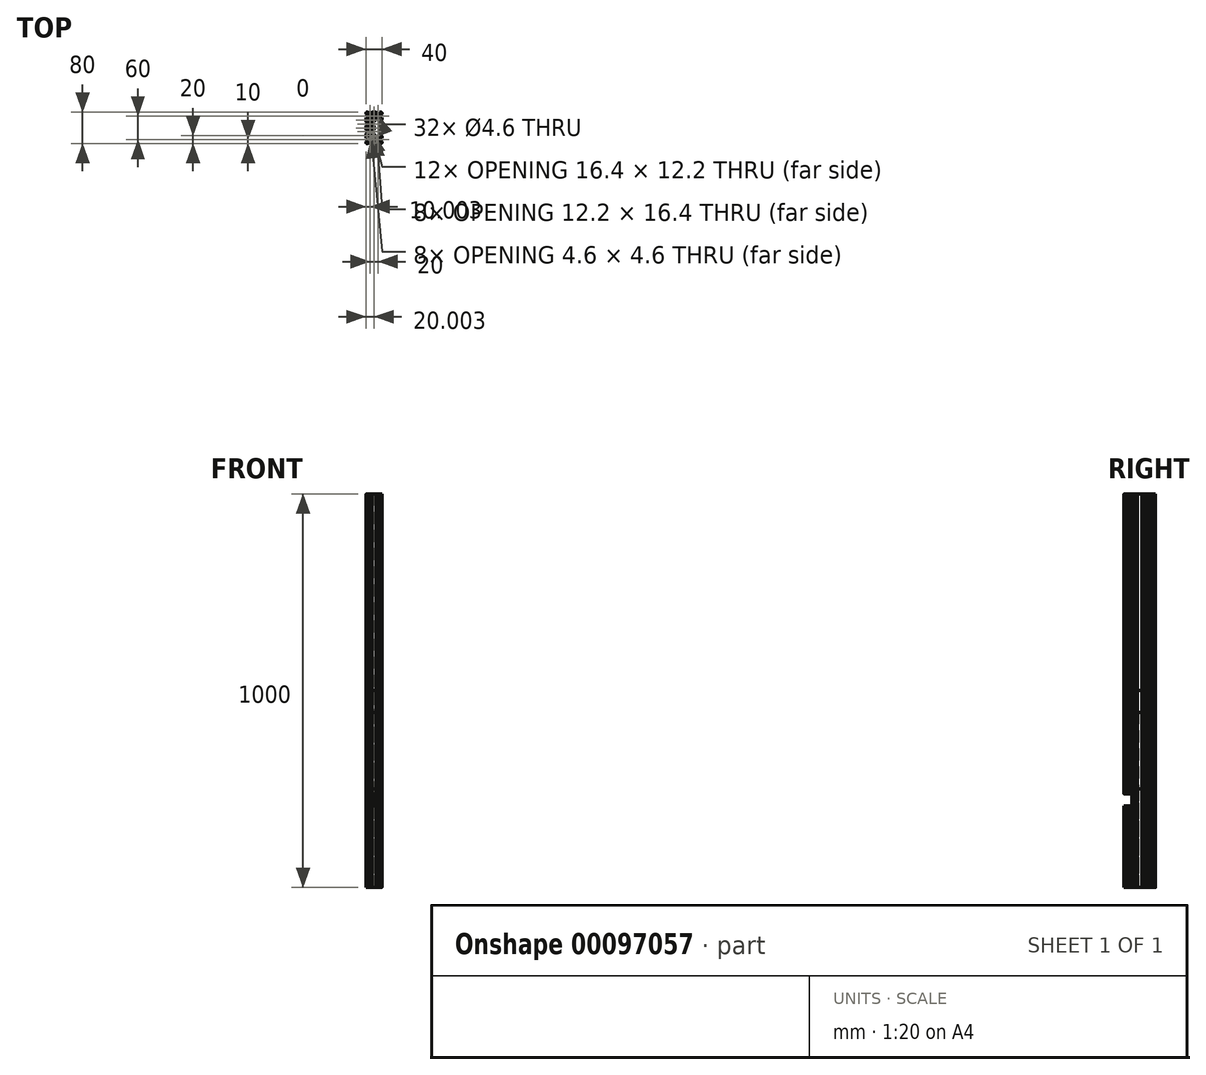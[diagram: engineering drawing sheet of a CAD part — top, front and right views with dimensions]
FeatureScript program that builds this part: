
annotation { "Feature Type Name" : "Feature", "Feature Type Description" : "" }
export const myFeature = defineFeature(function(context is Context, id is Id, definition is map)
    precondition{}
    {
        {
            var Q0;
            Q0=qCreatedBy(makeId("Top.planeOp"),FACE);
            var sketch = newSketch(context, id + "F0", { "sketchPlane" : qUnion([Q0])});
            skLineSegment(sketch, "E0", {"start": v(-12.56, -40) * mm, "end": v(-11.37, -38.82) * mm});
            skLineSegment(sketch, "E1", {"start": v(-11.37, -38.82) * mm, "end": v(-11.37, -38.2) * mm});
            skLineSegment(sketch, "E2", {"start": v(-11.37, -38.2) * mm, "end": v(-13.48, -38.2) * mm});
            skLineSegment(sketch, "E3", {"start": v(-13.48, -38.2) * mm, "end": v(-13.48, -36.56) * mm});
            skLineSegment(sketch, "E4", {"start": v(-13.48, -36.56) * mm, "end": v(-10.82, -33.9) * mm});
            skLineSegment(sketch, "E5", {"start": v(-10.82, -33.9) * mm, "end": v(-8.19, -33.9) * mm});
            skLineSegment(sketch, "E6", {"start": v(-8.19, -33.9) * mm, "end": v(-7.98, -33.69) * mm});
            skLineSegment(sketch, "E7", {"start": v(-7.98, -33.69) * mm, "end": v(-7.77, -33.9) * mm});
            skLineSegment(sketch, "E8", {"start": v(-7.77, -33.9) * mm, "end": v(-5.14, -33.9) * mm});
            skLineSegment(sketch, "E9", {"start": v(-5.14, -33.9) * mm, "end": v(-2.48, -36.56) * mm});
            skLineSegment(sketch, "E10", {"start": v(-2.48, -36.56) * mm, "end": v(-2.48, -38.2) * mm});
            skLineSegment(sketch, "E11", {"start": v(-2.48, -38.2) * mm, "end": v(-4.58, -38.2) * mm});
            skLineSegment(sketch, "E12", {"start": v(-4.58, -38.2) * mm, "end": v(-4.58, -38.82) * mm});
            skLineSegment(sketch, "E13", {"start": v(-4.58, -38.82) * mm, "end": v(-3.4, -40) * mm});
            skLineSegment(sketch, "E14", {"start": v(-3.4, -40) * mm, "end": v(7.44, -40) * mm});
            skLineSegment(sketch, "E15", {"start": v(7.44, -40) * mm, "end": v(8.63, -38.82) * mm});
            skLineSegment(sketch, "E16", {"start": v(8.63, -38.82) * mm, "end": v(8.63, -38.2) * mm});
            skLineSegment(sketch, "E17", {"start": v(8.63, -38.2) * mm, "end": v(6.52, -38.2) * mm});
            skLineSegment(sketch, "E18", {"start": v(6.52, -38.2) * mm, "end": v(6.52, -36.56) * mm});
            skLineSegment(sketch, "E19", {"start": v(6.52, -36.56) * mm, "end": v(9.18, -33.9) * mm});
            skLineSegment(sketch, "E20", {"start": v(9.18, -33.9) * mm, "end": v(11.81, -33.9) * mm});
            skLineSegment(sketch, "E21", {"start": v(11.81, -33.9) * mm, "end": v(12.02, -33.69) * mm});
            skLineSegment(sketch, "E22", {"start": v(12.02, -33.7) * mm, "end": v(12.23, -33.9) * mm});
            skLineSegment(sketch, "E23", {"start": v(12.23, -33.9) * mm, "end": v(14.86, -33.9) * mm});
            skLineSegment(sketch, "E24", {"start": v(14.86, -33.9) * mm, "end": v(17.52, -36.56) * mm});
            skLineSegment(sketch, "E25", {"start": v(17.52, -36.56) * mm, "end": v(17.52, -38.2) * mm});
            skLineSegment(sketch, "E26", {"start": v(17.52, -38.2) * mm, "end": v(15.42, -38.2) * mm});
            skLineSegment(sketch, "E27", {"start": v(15.42, -38.2) * mm, "end": v(15.42, -38.82) * mm});
            skLineSegment(sketch, "E28", {"start": v(15.42, -38.82) * mm, "end": v(16.6, -40) * mm});
            skLineSegment(sketch, "E29", {"start": v(16.6, -40) * mm, "end": v(20.52, -40) * mm});
            skLineSegment(sketch, "E30", {"start": v(22.02, -38.5) * mm, "end": v(22.02, -34.58) * mm});
            skLineSegment(sketch, "E31", {"start": v(22.02, -34.58) * mm, "end": v(20.84, -33.4) * mm});
            skLineSegment(sketch, "E32", {"start": v(20.84, -33.4) * mm, "end": v(20.22, -33.4) * mm});
            skLineSegment(sketch, "E33", {"start": v(20.22, -33.4) * mm, "end": v(20.22, -35.5) * mm});
            skLineSegment(sketch, "E34", {"start": v(20.22, -35.5) * mm, "end": v(18.58, -35.5) * mm});
            skLineSegment(sketch, "E35", {"start": v(18.58, -35.5) * mm, "end": v(15.92, -32.84) * mm});
            skLineSegment(sketch, "E36", {"start": v(15.92, -32.84) * mm, "end": v(15.92, -30.21) * mm});
            skLineSegment(sketch, "E37", {"start": v(15.92, -30.21) * mm, "end": v(15.71, -30) * mm});
            skLineSegment(sketch, "E38", {"start": v(15.71, -30) * mm, "end": v(15.92, -29.79) * mm});
            skLineSegment(sketch, "E39", {"start": v(15.92, -29.79) * mm, "end": v(15.92, -27.16) * mm});
            skLineSegment(sketch, "E40", {"start": v(15.92, -27.16) * mm, "end": v(18.58, -24.5) * mm});
            skLineSegment(sketch, "E41", {"start": v(18.58, -24.5) * mm, "end": v(20.22, -24.5) * mm});
            skLineSegment(sketch, "E42", {"start": v(20.22, -24.5) * mm, "end": v(20.22, -26.6) * mm});
            skLineSegment(sketch, "E43", {"start": v(20.22, -26.6) * mm, "end": v(20.84, -26.6) * mm});
            skLineSegment(sketch, "E44", {"start": v(20.84, -26.6) * mm, "end": v(22.02, -25.42) * mm});
            skLineSegment(sketch, "E45", {"start": v(22.02, -25.42) * mm, "end": v(22.02, -21.5) * mm});
            skLineSegment(sketch, "E46", {"start": v(20.52, -20) * mm, "end": v(16.6, -20) * mm});
            skLineSegment(sketch, "E47", {"start": v(16.6, -20) * mm, "end": v(15.42, -21.18) * mm});
            skLineSegment(sketch, "E48", {"start": v(15.42, -21.18) * mm, "end": v(15.42, -21.8) * mm});
            skLineSegment(sketch, "E49", {"start": v(15.42, -21.8) * mm, "end": v(17.52, -21.8) * mm});
            skLineSegment(sketch, "E50", {"start": v(17.52, -21.8) * mm, "end": v(17.52, -23.44) * mm});
            skLineSegment(sketch, "E51", {"start": v(17.52, -23.44) * mm, "end": v(14.86, -26.1) * mm});
            skLineSegment(sketch, "E52", {"start": v(14.86, -26.1) * mm, "end": v(12.23, -26.1) * mm});
            skLineSegment(sketch, "E53", {"start": v(12.23, -26.1) * mm, "end": v(12.02, -26.3) * mm});
            skLineSegment(sketch, "E54", {"start": v(12.02, -26.3) * mm, "end": v(11.81, -26.1) * mm});
            skLineSegment(sketch, "E55", {"start": v(11.81, -26.1) * mm, "end": v(9.18, -26.1) * mm});
            skLineSegment(sketch, "E56", {"start": v(9.18, -26.1) * mm, "end": v(6.52, -23.44) * mm});
            skLineSegment(sketch, "E57", {"start": v(6.52, -23.44) * mm, "end": v(6.52, -21.8) * mm});
            skLineSegment(sketch, "E58", {"start": v(-12.56, -40) * mm, "end": v(-16.48, -40) * mm});
            skLineSegment(sketch, "E59", {"start": v(6.52, -21.8) * mm, "end": v(8.63, -21.8) * mm});
            skLineSegment(sketch, "E60", {"start": v(-17.98, -38.5) * mm, "end": v(-17.98, -34.58) * mm});
            skLineSegment(sketch, "E61", {"start": v(8.63, -21.8) * mm, "end": v(8.63, -21.18) * mm});
            skLineSegment(sketch, "E62", {"start": v(-17.98, -34.58) * mm, "end": v(-16.8, -33.4) * mm});
            skLineSegment(sketch, "E63", {"start": v(8.63, -21.18) * mm, "end": v(7.44, -20) * mm});
            skLineSegment(sketch, "E64", {"start": v(-16.8, -33.4) * mm, "end": v(-16.18, -33.4) * mm});
            skLineSegment(sketch, "E65", {"start": v(7.44, -20) * mm, "end": v(2.02, -20) * mm});
            skLineSegment(sketch, "E66", {"start": v(-16.18, -33.4) * mm, "end": v(-16.18, -35.5) * mm});
            skLineSegment(sketch, "E67", {"start": v(2.02, -20) * mm, "end": v(2.02, -14.58) * mm});
            skLineSegment(sketch, "E68", {"start": v(-16.18, -35.5) * mm, "end": v(-14.54, -35.5) * mm});
            skLineSegment(sketch, "E69", {"start": v(2.02, -14.58) * mm, "end": v(0.84, -13.4) * mm});
            skLineSegment(sketch, "E70", {"start": v(-14.54, -35.5) * mm, "end": v(-11.88, -32.84) * mm});
            skLineSegment(sketch, "E71", {"start": v(0.84, -13.4) * mm, "end": v(0.22, -13.4) * mm});
            skLineSegment(sketch, "E72", {"start": v(-11.88, -32.84) * mm, "end": v(-11.88, -30.21) * mm});
            skLineSegment(sketch, "E73", {"start": v(0.22, -13.4) * mm, "end": v(0.22, -15.5) * mm});
            skLineSegment(sketch, "E74", {"start": v(-11.88, -30.21) * mm, "end": v(-11.67, -30) * mm});
            skLineSegment(sketch, "E75", {"start": v(0.22, -15.5) * mm, "end": v(-1.42, -15.5) * mm});
            skLineSegment(sketch, "E76", {"start": v(-11.67, -30) * mm, "end": v(-11.88, -29.79) * mm});
            skLineSegment(sketch, "E77", {"start": v(-1.42, -15.5) * mm, "end": v(-4.08, -12.84) * mm});
            skLineSegment(sketch, "E78", {"start": v(-11.88, -29.79) * mm, "end": v(-11.88, -27.16) * mm});
            skLineSegment(sketch, "E79", {"start": v(-4.08, -12.84) * mm, "end": v(-4.08, -10.21) * mm});
            skLineSegment(sketch, "E80", {"start": v(-11.88, -27.16) * mm, "end": v(-14.54, -24.5) * mm});
            skLineSegment(sketch, "E81", {"start": v(-4.08, -10.21) * mm, "end": v(-4.29, -10) * mm});
            skLineSegment(sketch, "E82", {"start": v(-14.54, -24.5) * mm, "end": v(-16.18, -24.5) * mm});
            skLineSegment(sketch, "E83", {"start": v(-4.29, -10) * mm, "end": v(-4.08, -9.8) * mm});
            skLineSegment(sketch, "E84", {"start": v(-16.18, -24.5) * mm, "end": v(-16.18, -26.6) * mm});
            skLineSegment(sketch, "E85", {"start": v(-4.08, -9.8) * mm, "end": v(-4.08, -7.16) * mm});
            skLineSegment(sketch, "E86", {"start": v(-16.18, -26.6) * mm, "end": v(-16.8, -26.6) * mm});
            skLineSegment(sketch, "E87", {"start": v(-4.08, -7.16) * mm, "end": v(-1.42, -4.5) * mm});
            skLineSegment(sketch, "E88", {"start": v(-16.8, -26.6) * mm, "end": v(-17.98, -25.42) * mm});
            skLineSegment(sketch, "E89", {"start": v(-1.42, -4.5) * mm, "end": v(0.22, -4.5) * mm});
            skLineSegment(sketch, "E90", {"start": v(-17.98, -25.42) * mm, "end": v(-17.98, -14.58) * mm});
            skLineSegment(sketch, "E91", {"start": v(0.22, -4.5) * mm, "end": v(0.22, -6.6) * mm});
            skLineSegment(sketch, "E92", {"start": v(-17.98, -14.58) * mm, "end": v(-16.8, -13.4) * mm});
            skLineSegment(sketch, "E93", {"start": v(0.22, -6.6) * mm, "end": v(0.84, -6.6) * mm});
            skLineSegment(sketch, "E94", {"start": v(-16.8, -13.4) * mm, "end": v(-16.18, -13.4) * mm});
            skLineSegment(sketch, "E95", {"start": v(0.84, -6.6) * mm, "end": v(2.02, -5.42) * mm});
            skLineSegment(sketch, "E96", {"start": v(-16.18, -13.4) * mm, "end": v(-16.18, -15.5) * mm});
            skLineSegment(sketch, "E97", {"start": v(2.02, -5.42) * mm, "end": v(2.02, 0) * mm});
            skLineSegment(sketch, "E98", {"start": v(-16.18, -15.5) * mm, "end": v(-14.54, -15.5) * mm});
            skLineSegment(sketch, "E99", {"start": v(-14.54, -15.5) * mm, "end": v(-11.88, -12.84) * mm});
            skLineSegment(sketch, "E100", {"start": v(-11.88, -12.84) * mm, "end": v(-11.88, -10.21) * mm});
            skLineSegment(sketch, "E101", {"start": v(-11.88, -10.21) * mm, "end": v(-11.67, -10) * mm});
            skLineSegment(sketch, "E102", {"start": v(-11.67, -10) * mm, "end": v(-11.88, -9.8) * mm});
            skLineSegment(sketch, "E103", {"start": v(-11.88, -9.8) * mm, "end": v(-11.88, -7.16) * mm});
            skLineSegment(sketch, "E104", {"start": v(-11.88, -7.16) * mm, "end": v(-14.54, -4.5) * mm});
            skLineSegment(sketch, "E105", {"start": v(-14.54, -4.5) * mm, "end": v(-16.18, -4.5) * mm});
            skLineSegment(sketch, "E106", {"start": v(-16.18, -4.5) * mm, "end": v(-16.18, -6.6) * mm});
            skLineSegment(sketch, "E107", {"start": v(-16.18, -6.6) * mm, "end": v(-16.8, -6.6) * mm});
            skLineSegment(sketch, "E108", {"start": v(-16.8, -6.6) * mm, "end": v(-17.98, -5.42) * mm});
            skLineSegment(sketch, "E109", {"start": v(-17.98, -5.42) * mm, "end": v(-17.98, 0) * mm});
            skLineSegment(sketch, "E110", {"start": v(-0.68, -38.2) * mm, "end": v(4.72, -38.2) * mm});
            skLineSegment(sketch, "E111", {"start": v(4.72, -38.2) * mm, "end": v(4.72, -36.24) * mm});
            skLineSegment(sketch, "E112", {"start": v(4.72, -36.24) * mm, "end": v(8.12, -32.84) * mm});
            skLineSegment(sketch, "E113", {"start": v(8.12, -32.84) * mm, "end": v(8.12, -27.16) * mm});
            skLineSegment(sketch, "E114", {"start": v(8.12, -27.16) * mm, "end": v(4.72, -23.76) * mm});
            skLineSegment(sketch, "E115", {"start": v(4.72, -23.76) * mm, "end": v(4.72, -21.8) * mm});
            skLineSegment(sketch, "E116", {"start": v(4.72, -21.8) * mm, "end": v(1.28, -21.8) * mm});
            skLineSegment(sketch, "E117", {"start": v(1.28, -21.8) * mm, "end": v(-4.08, -27.16) * mm});
            skLineSegment(sketch, "E118", {"start": v(-4.08, -27.16) * mm, "end": v(-4.08, -32.84) * mm});
            skLineSegment(sketch, "E119", {"start": v(-4.08, -32.84) * mm, "end": v(-0.68, -36.24) * mm});
            skLineSegment(sketch, "E120", {"start": v(-0.68, -36.24) * mm, "end": v(-0.68, -38.2) * mm});
            skLineSegment(sketch, "E121", {"start": v(-10.82, -26.1) * mm, "end": v(-5.14, -26.1) * mm});
            skLineSegment(sketch, "E122", {"start": v(-5.14, -26.1) * mm, "end": v(0.22, -20.74) * mm});
            skLineSegment(sketch, "E123", {"start": v(0.22, -20.74) * mm, "end": v(0.22, -17.3) * mm});
            skLineSegment(sketch, "E124", {"start": v(0.22, -17.3) * mm, "end": v(-1.74, -17.3) * mm});
            skLineSegment(sketch, "E125", {"start": v(-1.74, -17.3) * mm, "end": v(-5.14, -13.9) * mm});
            skLineSegment(sketch, "E126", {"start": v(-5.14, -13.9) * mm, "end": v(-10.82, -13.9) * mm});
            skLineSegment(sketch, "E127", {"start": v(-10.82, -13.9) * mm, "end": v(-14.22, -17.3) * mm});
            skLineSegment(sketch, "E128", {"start": v(-14.22, -17.3) * mm, "end": v(-16.18, -17.3) * mm});
            skLineSegment(sketch, "E129", {"start": v(-16.18, -17.3) * mm, "end": v(-16.18, -22.7) * mm});
            skLineSegment(sketch, "E130", {"start": v(-16.18, -22.7) * mm, "end": v(-14.22, -22.7) * mm});
            skLineSegment(sketch, "E131", {"start": v(-14.22, -22.7) * mm, "end": v(-10.82, -26.1) * mm});
            skLineSegment(sketch, "E132", {"start": v(-16.18, 0) * mm, "end": v(-16.18, -2.7) * mm});
            skLineSegment(sketch, "E133", {"start": v(-16.18, -2.7) * mm, "end": v(-14.22, -2.7) * mm});
            skLineSegment(sketch, "E134", {"start": v(-14.22, -2.7) * mm, "end": v(-10.82, -6.1) * mm});
            skLineSegment(sketch, "E135", {"start": v(-10.82, -6.1) * mm, "end": v(-5.14, -6.1) * mm});
            skLineSegment(sketch, "E136", {"start": v(-5.14, -6.1) * mm, "end": v(-1.74, -2.7) * mm});
            skLineSegment(sketch, "E137", {"start": v(-1.74, -2.7) * mm, "end": v(0.22, -2.7) * mm});
            skLineSegment(sketch, "E138", {"start": v(0.22, -2.7) * mm, "end": v(0.22, 0) * mm});
            skCircle(sketch, "E139", {"center": v(-7.98, -10) * mm, "radius": 2.3 * mm});
            skPoint(sketch, "E139.first.point", {"position": v(-9.64, -11.59) * mm});
            skPoint(sketch, "E139.second.point", {"position": v(-5.77, -10.63) * mm});
            skPoint(sketch, "E139.third.point", {"position": v(-6.97, -7.93) * mm});
            skCircle(sketch, "E140", {"center": v(-7.98, -30) * mm, "radius": 2.3 * mm});
            skPoint(sketch, "E140.first.point", {"position": v(-10.02, -31.05) * mm});
            skPoint(sketch, "E140.second.point", {"position": v(-6.08, -31.3) * mm});
            skPoint(sketch, "E140.third.point", {"position": v(-6.51, -28.23) * mm});
            skCircle(sketch, "E141", {"center": v(12.02, -30) * mm, "radius": 2.3 * mm});
            skPoint(sketch, "E141.first.point", {"position": v(9.96, -31) * mm});
            skPoint(sketch, "E141.second.point", {"position": v(14.22, -30.67) * mm});
            skPoint(sketch, "E141.third.point", {"position": v(13.22, -28.04) * mm});
            skLineSegment(sketch, "E142", {"start": v(-28.08, 0) * mm, "end": v(32.1, 0) * mm, "construction": true});
            skLineSegment(sketch, "E143.MirrorCS", {"start": v(-8.19, 33.9) * mm, "end": v(-7.98, 33.69) * mm});
            skLineSegment(sketch, "E144.MirrorCS", {"start": v(-11.67, 10) * mm, "end": v(-11.88, 9.79) * mm});
            skLineSegment(sketch, "E145.MirrorCS", {"start": v(-7.98, 33.69) * mm, "end": v(-7.77, 33.9) * mm});
            skLineSegment(sketch, "E146.MirrorCS", {"start": v(-11.88, 10.2) * mm, "end": v(-11.67, 10) * mm});
            skLineSegment(sketch, "E147.MirrorCS", {"start": v(-4.29, 10) * mm, "end": v(-4.08, 9.8) * mm});
            skLineSegment(sketch, "E148.MirrorCS", {"start": v(17.52, 38.2) * mm, "end": v(15.42, 38.2) * mm});
            skLineSegment(sketch, "E149.MirrorCS", {"start": v(-16.18, 4.5) * mm, "end": v(-16.18, 6.6) * mm});
            skLineSegment(sketch, "E150.MirrorCS", {"start": v(-11.88, 30.2) * mm, "end": v(-11.67, 30) * mm});
            skLineSegment(sketch, "E151.MirrorCS", {"start": v(-14.54, 24.5) * mm, "end": v(-16.18, 24.5) * mm});
            skLineSegment(sketch, "E152.MirrorCS", {"start": v(-16.18, 15.5) * mm, "end": v(-14.54, 15.5) * mm});
            skLineSegment(sketch, "E153.MirrorCS", {"start": v(-16.18, 22.7) * mm, "end": v(-14.22, 22.7) * mm});
            skLineSegment(sketch, "E154.MirrorCS", {"start": v(6.52, 38.2) * mm, "end": v(6.52, 36.56) * mm});
            skLineSegment(sketch, "E155.MirrorCS", {"start": v(20.22, 35.5) * mm, "end": v(18.58, 35.5) * mm});
            skLineSegment(sketch, "E156.MirrorCS", {"start": v(17.52, 21.8) * mm, "end": v(17.52, 23.44) * mm});
            skLineSegment(sketch, "E157.MirrorCS", {"start": v(4.72, 23.76) * mm, "end": v(4.72, 21.8) * mm});
            skLineSegment(sketch, "E158.MirrorCS", {"start": v(-16.18, 33.4) * mm, "end": v(-16.18, 35.5) * mm});
            skLineSegment(sketch, "E159.MirrorCS", {"start": v(-1.74, 2.7) * mm, "end": v(0.22, 2.7) * mm});
            skLineSegment(sketch, "E160.MirrorCS", {"start": v(6.52, 23.44) * mm, "end": v(6.52, 21.8) * mm});
            skLineSegment(sketch, "E161.MirrorCS", {"start": v(0.22, 13.4) * mm, "end": v(0.22, 15.5) * mm});
            skLineSegment(sketch, "E162.MirrorCS", {"start": v(-1.42, 4.5) * mm, "end": v(0.22, 4.5) * mm});
            skLineSegment(sketch, "E163.MirrorCS", {"start": v(-14.54, 4.5) * mm, "end": v(-16.18, 4.5) * mm});
            skLineSegment(sketch, "E164.MirrorCS", {"start": v(17.52, 36.56) * mm, "end": v(17.52, 38.2) * mm});
            skLineSegment(sketch, "E165.MirrorCS", {"start": v(18.58, 24.5) * mm, "end": v(20.22, 24.5) * mm});
            skLineSegment(sketch, "E166.MirrorCS", {"start": v(-4.08, 10.21) * mm, "end": v(-4.29, 10) * mm});
            skLineSegment(sketch, "E167.MirrorCS", {"start": v(-16.8, 26.6) * mm, "end": v(-17.98, 25.42) * mm});
            skLineSegment(sketch, "E168.MirrorCS", {"start": v(-4.58, 38.2) * mm, "end": v(-4.58, 38.82) * mm});
            skLineSegment(sketch, "E169.MirrorCS", {"start": v(-2.48, 38.2) * mm, "end": v(-4.58, 38.2) * mm});
            skLineSegment(sketch, "E170.MirrorCS", {"start": v(20.84, 33.4) * mm, "end": v(20.22, 33.4) * mm});
            skLineSegment(sketch, "E171.MirrorCS", {"start": v(-16.8, 33.4) * mm, "end": v(-16.18, 33.4) * mm});
            skLineSegment(sketch, "E172.MirrorCS", {"start": v(15.42, 21.18) * mm, "end": v(15.42, 21.8) * mm});
            skLineSegment(sketch, "E173.MirrorCS", {"start": v(-13.48, 38.2) * mm, "end": v(-13.48, 36.56) * mm});
            skLineSegment(sketch, "E174.MirrorCS", {"start": v(-11.37, 38.82) * mm, "end": v(-11.37, 38.2) * mm});
            skLineSegment(sketch, "E175.MirrorCS", {"start": v(-12.56, 40) * mm, "end": v(-11.37, 38.82) * mm});
            skLineSegment(sketch, "E176.MirrorCS", {"start": v(0.84, 13.4) * mm, "end": v(0.22, 13.4) * mm});
            skLineSegment(sketch, "E177.MirrorCS", {"start": v(7.44, 40) * mm, "end": v(8.63, 38.82) * mm});
            skLineSegment(sketch, "E178.MirrorCS", {"start": v(-4.58, 38.82) * mm, "end": v(-3.4, 40) * mm});
            skLineSegment(sketch, "E179.MirrorCS", {"start": v(-16.18, 13.4) * mm, "end": v(-16.18, 15.5) * mm});
            skLineSegment(sketch, "E180.MirrorCS", {"start": v(-14.22, 17.3) * mm, "end": v(-16.18, 17.3) * mm});
            skLineSegment(sketch, "E181.MirrorCS", {"start": v(-16.18, 26.6) * mm, "end": v(-16.8, 26.6) * mm});
            skLineSegment(sketch, "E182.MirrorCS", {"start": v(4.72, 38.2) * mm, "end": v(4.72, 36.24) * mm});
            skLineSegment(sketch, "E183.MirrorCS", {"start": v(0.84, 6.6) * mm, "end": v(2.02, 5.42) * mm});
            skLineSegment(sketch, "E184.MirrorCS", {"start": v(22.02, 34.58) * mm, "end": v(20.84, 33.4) * mm});
            skLineSegment(sketch, "E185.MirrorCS", {"start": v(12.02, 26.3) * mm, "end": v(11.81, 26.1) * mm});
            skLineSegment(sketch, "E186.MirrorCS", {"start": v(15.71, 30) * mm, "end": v(15.92, 29.79) * mm});
            skLineSegment(sketch, "E187.MirrorCS", {"start": v(8.63, 21.18) * mm, "end": v(7.44, 20) * mm});
            skLineSegment(sketch, "E188.MirrorCS", {"start": v(-11.67, 30) * mm, "end": v(-11.88, 29.79) * mm});
            skLineSegment(sketch, "E189.MirrorCS", {"start": v(-16.8, 6.6) * mm, "end": v(-17.98, 5.42) * mm});
            skLineSegment(sketch, "E190.MirrorCS", {"start": v(20.84, 26.6) * mm, "end": v(22.02, 25.42) * mm});
            skLineSegment(sketch, "E191.MirrorCS", {"start": v(8.63, 21.8) * mm, "end": v(8.63, 21.18) * mm});
            skLineSegment(sketch, "E192.MirrorCS", {"start": v(-16.18, 35.5) * mm, "end": v(-14.54, 35.5) * mm});
            skLineSegment(sketch, "E193.MirrorCS", {"start": v(0.22, 4.5) * mm, "end": v(0.22, 6.6) * mm});
            skLineSegment(sketch, "E194.MirrorCS", {"start": v(-16.18, 6.6) * mm, "end": v(-16.8, 6.6) * mm});
            skLineSegment(sketch, "E195.MirrorCS", {"start": v(20.22, 26.6) * mm, "end": v(20.84, 26.6) * mm});
            skLineSegment(sketch, "E196.MirrorCS", {"start": v(8.63, 38.2) * mm, "end": v(6.52, 38.2) * mm});
            skLineSegment(sketch, "E197.MirrorCS", {"start": v(15.42, 21.8) * mm, "end": v(17.52, 21.8) * mm});
            skLineSegment(sketch, "E198.MirrorCS", {"start": v(20.22, 33.4) * mm, "end": v(20.22, 35.5) * mm});
            skLineSegment(sketch, "E199.MirrorCS", {"start": v(-0.68, 36.24) * mm, "end": v(-0.68, 38.2) * mm});
            skLineSegment(sketch, "E200.MirrorCS", {"start": v(-2.48, 36.56) * mm, "end": v(-2.48, 38.2) * mm});
            skLineSegment(sketch, "E201.MirrorCS", {"start": v(8.63, 38.82) * mm, "end": v(8.63, 38.2) * mm});
            skLineSegment(sketch, "E202.MirrorCS", {"start": v(-11.37, 38.2) * mm, "end": v(-13.48, 38.2) * mm});
            skLineSegment(sketch, "E203.MirrorCS", {"start": v(12.02, 33.69) * mm, "end": v(12.23, 33.9) * mm});
            skLineSegment(sketch, "E204.MirrorCS", {"start": v(16.6, 20) * mm, "end": v(15.42, 21.18) * mm});
            skLineSegment(sketch, "E205.MirrorCS", {"start": v(-16.18, 2.7) * mm, "end": v(-14.22, 2.7) * mm});
            skLineSegment(sketch, "E206.MirrorCS", {"start": v(12.23, 26.1) * mm, "end": v(12.02, 26.3) * mm});
            skLineSegment(sketch, "E207.MirrorCS", {"start": v(-17.98, 14.58) * mm, "end": v(-16.8, 13.4) * mm});
            skLineSegment(sketch, "E208.MirrorCS", {"start": v(15.42, 38.82) * mm, "end": v(16.6, 40) * mm});
            skLineSegment(sketch, "E209.MirrorCS", {"start": v(20.22, 24.5) * mm, "end": v(20.22, 26.6) * mm});
            skLineSegment(sketch, "E210.MirrorCS", {"start": v(6.52, 21.8) * mm, "end": v(8.63, 21.8) * mm});
            skLineSegment(sketch, "E211.MirrorCS", {"start": v(0.22, 15.5) * mm, "end": v(-1.42, 15.5) * mm});
            skLineSegment(sketch, "E212.MirrorCS", {"start": v(-16.8, 13.4) * mm, "end": v(-16.18, 13.4) * mm});
            skLineSegment(sketch, "E213.MirrorCS", {"start": v(11.81, 33.9) * mm, "end": v(12.02, 33.69) * mm});
            skLineSegment(sketch, "E214.MirrorCS", {"start": v(15.92, 30.21) * mm, "end": v(15.71, 30) * mm});
            skLineSegment(sketch, "E215.MirrorCS", {"start": v(2.02, 14.58) * mm, "end": v(0.84, 13.4) * mm});
            skLineSegment(sketch, "E216.MirrorCS", {"start": v(-17.98, 34.58) * mm, "end": v(-16.8, 33.4) * mm});
            skLineSegment(sketch, "E217.MirrorCS", {"start": v(0.22, 17.3) * mm, "end": v(-1.74, 17.3) * mm});
            skLineSegment(sketch, "E218.MirrorCS", {"start": v(-16.18, 24.5) * mm, "end": v(-16.18, 26.6) * mm});
            skLineSegment(sketch, "E219.MirrorCS", {"start": v(0.22, 6.6) * mm, "end": v(0.84, 6.6) * mm});
            skLineSegment(sketch, "E220.MirrorCS", {"start": v(15.42, 38.2) * mm, "end": v(15.42, 38.82) * mm});
            skLineSegment(sketch, "E221.MirrorCS", {"start": v(-17.98, 25.42) * mm, "end": v(-17.98, 14.58) * mm});
            skLineSegment(sketch, "E222.MirrorCS", {"start": v(-12.56, 40) * mm, "end": v(-16.48, 40) * mm});
            skLineSegment(sketch, "E223.MirrorCS", {"start": v(0.22, 2.7) * mm, "end": v(0.22, 0) * mm});
            skLineSegment(sketch, "E224.MirrorCS", {"start": v(-5.14, 26.1) * mm, "end": v(0.22, 20.74) * mm});
            skPoint(sketch, "E225.MirrorP", {"position": v(13.22, 28.04) * mm});
            skLineSegment(sketch, "E226.MirrorCS", {"start": v(2.02, 20) * mm, "end": v(2.02, 14.58) * mm});
            skLineSegment(sketch, "E227.MirrorCS", {"start": v(17.52, 23.44) * mm, "end": v(14.86, 26.1) * mm});
            skLineSegment(sketch, "E228.MirrorCS", {"start": v(8.12, 27.16) * mm, "end": v(4.72, 23.76) * mm});
            skLineSegment(sketch, "E229.MirrorCS", {"start": v(18.58, 35.5) * mm, "end": v(15.92, 32.84) * mm});
            skLineSegment(sketch, "E230.MirrorCS", {"start": v(6.52, 36.56) * mm, "end": v(9.18, 33.9) * mm});
            skLineSegment(sketch, "E231.MirrorCS", {"start": v(-14.22, 22.7) * mm, "end": v(-10.82, 26.1) * mm});
            skLineSegment(sketch, "E232.MirrorCS", {"start": v(-14.54, 15.5) * mm, "end": v(-11.88, 12.84) * mm});
            skPoint(sketch, "E233.MirrorP", {"position": v(14.22, 30.67) * mm});
            skPoint(sketch, "E234.MirrorP", {"position": v(-5.77, 10.63) * mm});
            skLineSegment(sketch, "E235.MirrorCS", {"start": v(-10.82, 26.1) * mm, "end": v(-5.14, 26.1) * mm});
            skPoint(sketch, "E236.MirrorP", {"position": v(-9.64, 11.59) * mm});
            skLineSegment(sketch, "E237.MirrorCS", {"start": v(7.44, 20) * mm, "end": v(2.02, 20) * mm});
            skLineSegment(sketch, "E238.MirrorCS", {"start": v(-5.14, 6.1) * mm, "end": v(-1.74, 2.7) * mm});
            skLineSegment(sketch, "E239.MirrorCS", {"start": v(-11.88, 32.84) * mm, "end": v(-11.88, 30.21) * mm});
            skLineSegment(sketch, "E240.MirrorCS", {"start": v(15.92, 27.16) * mm, "end": v(18.58, 24.5) * mm});
            skLineSegment(sketch, "E241.MirrorCS", {"start": v(14.86, 33.9) * mm, "end": v(17.52, 36.56) * mm});
            skLineSegment(sketch, "E242.MirrorCS", {"start": v(-5.14, 33.9) * mm, "end": v(-2.48, 36.56) * mm});
            skLineSegment(sketch, "E243.MirrorCS", {"start": v(11.81, 26.1) * mm, "end": v(9.18, 26.1) * mm});
            skLineSegment(sketch, "E244.MirrorCS", {"start": v(-4.08, 7.16) * mm, "end": v(-1.42, 4.5) * mm});
            skLineSegment(sketch, "E245.MirrorCS", {"start": v(-11.88, 9.8) * mm, "end": v(-11.88, 7.16) * mm});
            skLineSegment(sketch, "E246.MirrorCS", {"start": v(12.23, 33.9) * mm, "end": v(14.86, 33.9) * mm});
            skLineSegment(sketch, "E247.MirrorCS", {"start": v(15.92, 29.79) * mm, "end": v(15.92, 27.16) * mm});
            skLineSegment(sketch, "E248.MirrorCS", {"start": v(-3.4, 40) * mm, "end": v(7.44, 40) * mm});
            skLineSegment(sketch, "E249.MirrorCS", {"start": v(-4.08, 12.84) * mm, "end": v(-4.08, 10.21) * mm});
            skLineSegment(sketch, "E250.MirrorCS", {"start": v(-4.08, 27.16) * mm, "end": v(-4.08, 32.84) * mm});
            skLineSegment(sketch, "E251.MirrorCS", {"start": v(-14.22, 2.7) * mm, "end": v(-10.82, 6.1) * mm});
            skLineSegment(sketch, "E252.MirrorCS", {"start": v(-10.82, 13.9) * mm, "end": v(-14.22, 17.3) * mm});
            skLineSegment(sketch, "E253.MirrorCS", {"start": v(-14.54, 35.5) * mm, "end": v(-11.88, 32.84) * mm});
            skLineSegment(sketch, "E254.MirrorCS", {"start": v(-5.14, 13.9) * mm, "end": v(-10.82, 13.9) * mm});
            skLineSegment(sketch, "E255.MirrorCS", {"start": v(1.28, 21.8) * mm, "end": v(-4.08, 27.16) * mm});
            skPoint(sketch, "E256.MirrorP", {"position": v(-6.08, 31.3) * mm});
            skPoint(sketch, "E257.MirrorP", {"position": v(-6.97, 7.93) * mm});
            skLineSegment(sketch, "E258.MirrorCS", {"start": v(-11.88, 12.84) * mm, "end": v(-11.88, 10.21) * mm});
            skLineSegment(sketch, "E259.MirrorCS", {"start": v(-16.18, 0) * mm, "end": v(-16.18, 2.7) * mm});
            skLineSegment(sketch, "E260.MirrorCS", {"start": v(-1.74, 17.3) * mm, "end": v(-5.14, 13.9) * mm});
            skLineSegment(sketch, "E261.MirrorCS", {"start": v(16.6, 40) * mm, "end": v(20.52, 40) * mm});
            skLineSegment(sketch, "E262.MirrorCS", {"start": v(22.02, 25.42) * mm, "end": v(22.02, 21.5) * mm});
            skLineSegment(sketch, "E263.MirrorCS", {"start": v(0.22, 20.74) * mm, "end": v(0.22, 17.3) * mm});
            skLineSegment(sketch, "E264.MirrorCS", {"start": v(8.12, 32.84) * mm, "end": v(8.12, 27.16) * mm});
            skLineSegment(sketch, "E265.MirrorCS", {"start": v(2.02, 5.42) * mm, "end": v(2.02, 0) * mm});
            skLineSegment(sketch, "E266.MirrorCS", {"start": v(-16.18, 17.3) * mm, "end": v(-16.18, 22.7) * mm});
            skPoint(sketch, "E267.MirrorP", {"position": v(9.96, 31) * mm});
            skLineSegment(sketch, "E268.MirrorCS", {"start": v(9.18, 26.1) * mm, "end": v(6.52, 23.44) * mm});
            skLineSegment(sketch, "E269.MirrorCS", {"start": v(-11.88, 7.16) * mm, "end": v(-14.54, 4.5) * mm});
            skLineSegment(sketch, "E270.MirrorCS", {"start": v(-4.08, 32.84) * mm, "end": v(-0.68, 36.24) * mm});
            skLineSegment(sketch, "E271.MirrorCS", {"start": v(-10.82, 6.1) * mm, "end": v(-5.14, 6.1) * mm});
            skLineSegment(sketch, "E272.MirrorCS", {"start": v(-7.77, 33.9) * mm, "end": v(-5.14, 33.9) * mm});
            skLineSegment(sketch, "E273.MirrorCS", {"start": v(-10.82, 33.9) * mm, "end": v(-8.19, 33.9) * mm});
            skLineSegment(sketch, "E274.MirrorCS", {"start": v(-13.48, 36.56) * mm, "end": v(-10.82, 33.9) * mm});
            skLineSegment(sketch, "E275.MirrorCS", {"start": v(-11.88, 27.16) * mm, "end": v(-14.54, 24.5) * mm});
            skLineSegment(sketch, "E276.MirrorCS", {"start": v(4.72, 36.24) * mm, "end": v(8.12, 32.84) * mm});
            skPoint(sketch, "E277.MirrorP", {"position": v(-6.51, 28.23) * mm});
            skLineSegment(sketch, "E278.MirrorCS", {"start": v(-11.88, 29.79) * mm, "end": v(-11.88, 27.16) * mm});
            skLineSegment(sketch, "E279.MirrorCS", {"start": v(20.52, 20) * mm, "end": v(16.6, 20) * mm});
            skLineSegment(sketch, "E280.MirrorCS", {"start": v(-17.98, 38.5) * mm, "end": v(-17.98, 34.58) * mm});
            skCircle(sketch, "E281.MirrorC", {"center": v(-7.98, 30) * mm, "radius": 2.3 * mm});
            skLineSegment(sketch, "E282.MirrorCS", {"start": v(4.72, 21.8) * mm, "end": v(1.28, 21.8) * mm});
            skLineSegment(sketch, "E283.MirrorCS", {"start": v(-17.98, 5.42) * mm, "end": v(-17.98, 0) * mm});
            skLineSegment(sketch, "E284.MirrorCS", {"start": v(9.18, 33.9) * mm, "end": v(11.81, 33.9) * mm});
            skLineSegment(sketch, "E285.MirrorCS", {"start": v(15.92, 32.84) * mm, "end": v(15.92, 30.21) * mm});
            skLineSegment(sketch, "E286.MirrorCS", {"start": v(14.86, 26.1) * mm, "end": v(12.23, 26.1) * mm});
            skCircle(sketch, "E287.MirrorC", {"center": v(-7.98, 10) * mm, "radius": 2.3 * mm});
            skLineSegment(sketch, "E288.MirrorCS", {"start": v(-4.08, 9.8) * mm, "end": v(-4.08, 7.16) * mm});
            skLineSegment(sketch, "E289.MirrorCS", {"start": v(-0.68, 38.2) * mm, "end": v(4.72, 38.2) * mm});
            skLineSegment(sketch, "E290.MirrorCS", {"start": v(22.02, 38.5) * mm, "end": v(22.02, 34.58) * mm});
            skCircle(sketch, "E291.MirrorC", {"center": v(12.02, 30) * mm, "radius": 2.3 * mm});
            skLineSegment(sketch, "E292.MirrorCS", {"start": v(-1.42, 15.5) * mm, "end": v(-4.08, 12.84) * mm});
            skPoint(sketch, "E293.MirrorP", {"position": v(-10.02, 31.05) * mm});
            skPoint(sketch, "E294.visualSharp", {"position": v(-17.98, -40) * mm});
            skArc(sketch, "E294.filletArc", {"start": v(-17.98, -38.5) * mm, "mid": v(-17.54, -39.56) * mm, "end": v(-16.48, -40) * mm});
            skPoint(sketch, "E295.visualSharp", {"position": v(22.02, -40) * mm});
            skArc(sketch, "E295.filletArc", {"start": v(20.52, -40) * mm, "mid": v(21.58, -39.56) * mm, "end": v(22.02, -38.5) * mm});
            skPoint(sketch, "E296.visualSharp", {"position": v(22.02, -20) * mm});
            skArc(sketch, "E296.filletArc", {"start": v(22.02, -21.5) * mm, "mid": v(21.58, -20.44) * mm, "end": v(20.52, -20) * mm});
            skPoint(sketch, "E297.visualSharp", {"position": v(-17.98, 40) * mm});
            skArc(sketch, "E297.filletArc", {"start": v(-16.48, 40) * mm, "mid": v(-17.54, 39.56) * mm, "end": v(-17.98, 38.5) * mm});
            skPoint(sketch, "E298.visualSharp", {"position": v(22.02, 40) * mm});
            skArc(sketch, "E298.filletArc", {"start": v(22.02, 38.5) * mm, "mid": v(21.58, 39.56) * mm, "end": v(20.52, 40) * mm});
            skPoint(sketch, "E299.visualSharp", {"position": v(22.02, 20) * mm});
            skArc(sketch, "E299.filletArc", {"start": v(20.52, 20) * mm, "mid": v(21.58, 20.44) * mm, "end": v(22.02, 21.5) * mm});
            skSolve(sketch);
        }
        {
            var Q0;
            Q0=qSketchRegion(id+"F0",true);
            extrude(context, id + "F1", {"entities" : qUnion([Q0]), "depth" : 250 * mm});
        }
        {
            var Q0;
            Q0=qSketchRegion(id+"F0",true);
            extrude(context, id + "F2", {"entities" : qUnion([Q0]), "depth" : 500 * mm});
        }
        {
            var Q0;
            Q0=qSketchRegion(id+"F0",true);
            extrude(context, id + "F3", {"entities" : qUnion([Q0]), "depth" : 1000 * mm});
        }
        {
            var Q0;
            Q0=qSketchRegion(id+"F0",true);
            extrude(context, id + "F4", {"entities" : qUnion([Q0]), "depth" : 445 * mm});
        }
        {
            var Q0;
            Q0=qCreatedBy(makeId("Right.planeOp"),FACE);
            var sketch = newSketch(context, id + "F5", { "sketchPlane" : qUnion([Q0])});
            skLineSegment(sketch, "E300.bottom", {"start": v(-40, 237.5) * mm, "end": v(-22.5, 237.5) * mm});
            skLineSegment(sketch, "E300.top", {"start": v(-40, 207.5) * mm, "end": v(-22.5, 207.5) * mm});
            skLineSegment(sketch, "E300.left", {"start": v(-40, 237.5) * mm, "end": v(-40, 207.5) * mm});
            skLineSegment(sketch, "E300.right", {"start": v(-20, 235) * mm, "end": v(-20, 210) * mm});
            skPoint(sketch, "E301.visualSharp", {"position": v(-20, 237.5) * mm});
            skArc(sketch, "E301.filletArc", {"start": v(-20, 235) * mm, "mid": v(-20.73, 236.77) * mm, "end": v(-22.5, 237.5) * mm});
            skPoint(sketch, "E302.visualSharp", {"position": v(-20, 207.5) * mm});
            skArc(sketch, "E302.filletArc", {"start": v(-22.5, 207.5) * mm, "mid": v(-20.73, 208.23) * mm, "end": v(-20, 210) * mm});
            skLineSegment(sketch, "E303", {"start": v(-20, 222.5) * mm, "end": v(-40, 222.5) * mm, "construction": true});
            skSolve(sketch);
        }
        {
            var Q0;
            Q0=makeQuery(id+"F5.imprint","IMPRINT",FACE,{"disambiguationData":[TD([[makeQuery(id+"F5.imprint","IMPRINT",EDGE,{"derivedFrom":sQuery(id+"F5.wireOp",EDGE,"E300.bottom")}),-1.0]])]});
            extrude(context, id + "F6", {"entities" : qUnion([Q0]), "operationType" : NewBodyOperationType.REMOVE, "endBound" : BoundingType.THROUGH_ALL, "oppositeDirection" : true, "depth" : 25 * mm, "hasSecondDirection" : true, "secondDirectionBound" : SecondDirectionBoundingType.THROUGH_ALL, "secondDirectionOppositeDirection" : false, "secondDirectionDepth" : 25 * mm});
        }
    });
